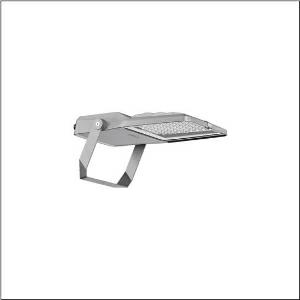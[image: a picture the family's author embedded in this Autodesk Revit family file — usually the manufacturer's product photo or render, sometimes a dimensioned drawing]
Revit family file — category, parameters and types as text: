
# Revit family: floodlight_fl_21_mini___pl64_5xa7775b2e1a_35e6
name_source: partatom
category: Lighting Fixtures
units: mm (PartAtom-declared; Revit-internal decimal feet)

## family parameters
Cut with Voids When Loaded = No
Host = Face
Light Source = No
Part Type = Normal
Room Calculation Point = No
Round Connector Dimension = Use Diameter
Shared = No

## types (1)
- --- (1 x LED, 6010 lm, 45.7 W, 3000K)
    Apparent Load = 46 VA
    CIE Flux Codes = 28 80 98 100 100
    Color Rendering = 70
    Color Temperature = 3000K
    Default Elevation = 1800 mm
    Description = Floodlight FL 21 mini, floodlight, primary light control with lens, of PMMA, primary optical cover: protective disc, of toughened safety glass, transparent, light distribution: PL64, light emission: direct distribution, installation type: surface-mounted, LED, High Power LED, rated luminous flux: 6.010lm, luminous efficacy: 132lm/W, light colour: 730, colour temperature: 3000K, control gear: Smart Interface (Zhaga), control: flexible luminous flux parameterisation, time-dependent luminous flux control, constant luminous flux control, overheat protection, pre-setting: logarithmic dimming characteristic, with terminal, 6-pole, mains connection: 220..240V, AC, 50/60Hz, start of lifetime: 46W, end of service life: 48W, reduction: 22W, luminaire housing, of diecast aluminium, powder-coated, SITECO metallic grey (DB 702S), corrosivity category C5 mid according to DIN EN ISO 12944, suitable for swimming pools, chlorine-resistant, sealing non-destructively replaceable, mounting bracket, of steel, galvanised, powder-coated, SITECO metallic grey (DB 702S), Smart Interface above, protection rating (complete): IP66, insulation class (complete): insulation class II (safety insulation), certification: CE, ENEC, VDE, protection symbol: D, impact resistance: IK08, permissible operating ambient temperature: -40..+40°C, permissible operating ambient temperature for outdoor applications: -40..+50°C, standard: DIN EN 12944, LABS conformity tested according to VDMA 24364:2018-05, packaging unit: 1 piece

Light Distribution: PL64
    Height = 70 mm
    Lamp = 1 x LED
    Lamp Light Flux = 6010 lm
    Lamp Power = 45.7 W
    Lamp count = 1
    Length = 485 mm
    Luminous efficacy = 132 lm/W
    Manufacturer = Siteco
    ModVariant = No
    Model = 5XA7775B2E1A
    Number of Poles = 1
    OnlyDefault = Yes
    Power Factor = 1
    Product Name = Floodlight FL 21 mini | PL64
    Product group = floodlight | pylon annexe
    ProductGroupID = 6201
    Protection Class = Protection class II
    Protection Degree = IP 66
    RLX_Detail_Level = 1
    RLX_Emergency_Light_Flux = 0 lm
    RLX_Emergency_Type = 0
    RLX_Emergency_Type_DB = No
    RlxData = <blob elided: 96061 chars, md5=565db61d>
    Socket = socket
    Standby Power = 0 W
    System Light Flux = 6010 lm
    System Power = 46 W
    Type Comments = factory setting: luminous flux: 100 % | dim-lin: 254 | 463 mA
    Type Image = l_1006845.jpg
    URL = http://relux.com
    VarID = @adj_165055
    Voltage = 0 V
    Weight = 0.00 kg
    Width = 337 mm

## geometry (parser evidence)
native form markers: Blend x4, Sweep x12
no freeform markers — native parametric forms only
